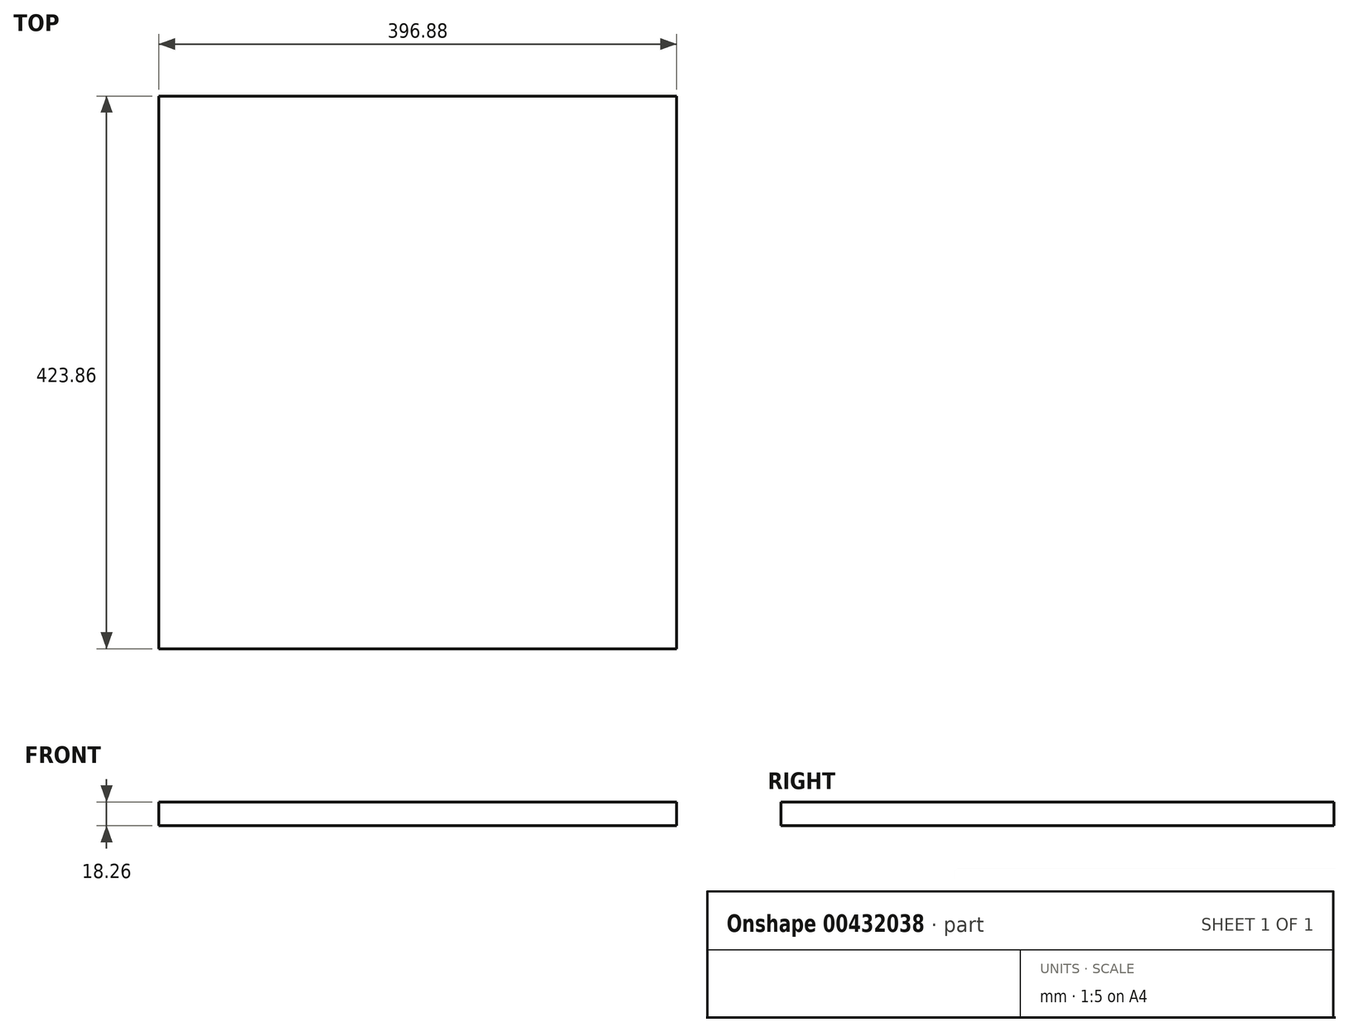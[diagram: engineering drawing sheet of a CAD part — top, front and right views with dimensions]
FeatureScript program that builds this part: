
annotation { "Feature Type Name" : "Feature", "Feature Type Description" : "" }
export const myFeature = defineFeature(function(context is Context, id is Id, definition is map)
    precondition{}
    {
        {
            var Q0;
            Q0=qCreatedBy(makeId("Top.planeOp"),FACE);
            var sketch = newSketch(context, id + "F0", { "sketchPlane" : qUnion([Q0])});
            skLineSegment(sketch, "E0.bottom", {"start": v(198.44, 211.93) * mm, "end": v(-198.44, 211.93) * mm});
            skLineSegment(sketch, "E0.top", {"start": v(198.44, -211.93) * mm, "end": v(-198.44, -211.93) * mm});
            skLineSegment(sketch, "E0.left", {"start": v(198.44, 211.93) * mm, "end": v(198.44, -211.93) * mm});
            skLineSegment(sketch, "E0.right", {"start": v(-198.44, 211.93) * mm, "end": v(-198.44, -211.93) * mm});
            skPoint(sketch, "E0.middle", {"position": v(0, 0) * mm});
            skSolve(sketch);
        }
        {
            var Q0;
            Q0=makeQuery(id+"F0.imprint","IMPRINT",FACE,{"disambiguationData":[TD([[makeQuery(id+"F0.imprint","IMPRINT",EDGE,{"derivedFrom":sQuery(id+"F0.wireOp",EDGE,"E0.bottom")}),1.0]])]});
            extrude(context, id + "F1", {"entities" : qUnion([Q0]), "depth" : 18.26 * mm});
        }
    });
